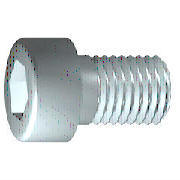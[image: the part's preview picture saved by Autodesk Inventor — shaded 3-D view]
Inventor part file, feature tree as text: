
AUTODESK INVENTOR PART (.ipt)
format: ipt  version: 2016 SP1 (Build 200210100, 210)  size: 199,168 bytes
history: native  units: mm (DEFAULTED — no unit token found)
features: sketch x2, extrude x1, plane x1, fillet x1
ambient origin geometry x7: Origin, YZ Plane, XY Plane, X Axis, Y Axis, Z Axis, Center Point
bodies: Solid1 (feature_tree), Body (feature_tree)
feature tree (5):
  extrude  "Slot"  Depth=3.5052mm
  plane  "Work Plane1"
  fillet  "Fillet2"  Radius=3.5052mm
  sketch  "Sketch1"  dims[d1=7.540552mm d2=1.984348mm d3=3.5052mm]
  sketch  "Sketch2"  dims[d4=1.6256mm d5=60.0deg d6=3.5052mm d7=3.5052mm d8=3.196904mm d9=5.7404mm d10=90.0deg d11=10.0mm d12=0.0mm d13=7.540552mm d14=0.0mm d15=0.47244mm d16=0.47244mm d17=0.3302mm d19=0.0mm d26=9.525mm d27=45.0deg d28=0.0mm d29=0.0mm d30=0.127mm]
